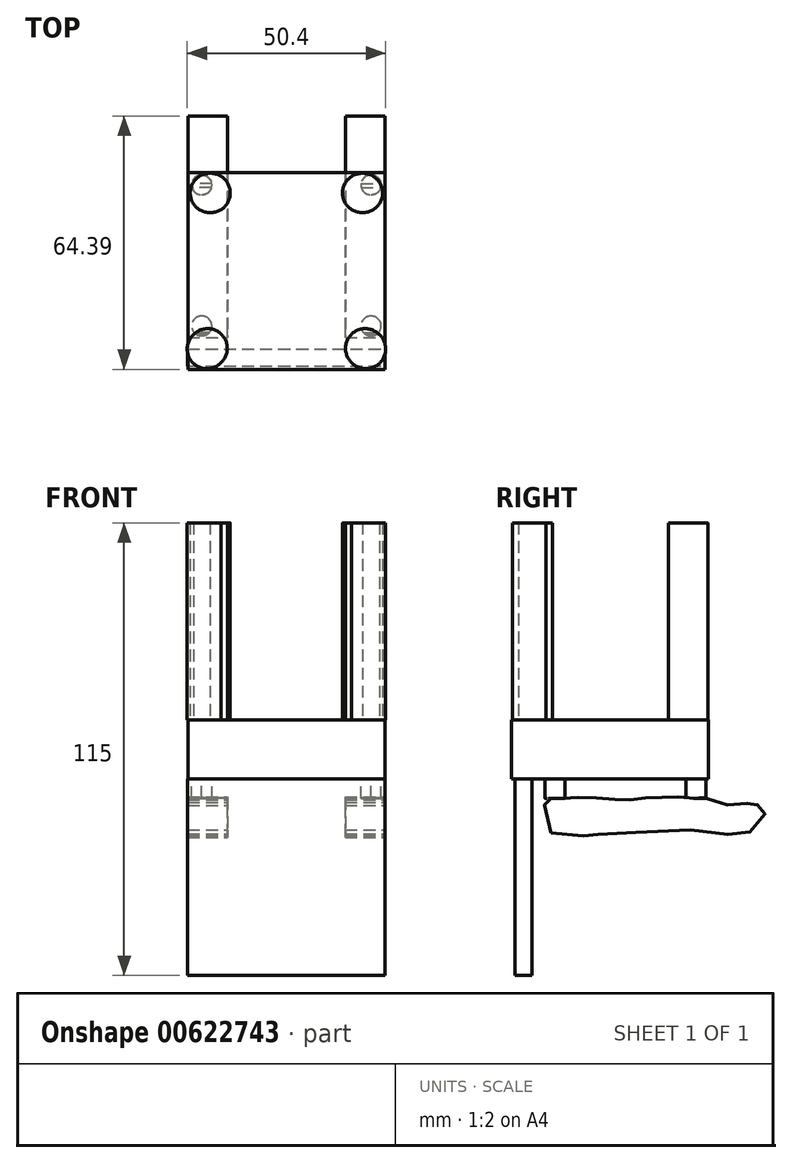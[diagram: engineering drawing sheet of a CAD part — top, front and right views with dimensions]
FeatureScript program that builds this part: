
annotation { "Feature Type Name" : "Feature", "Feature Type Description" : "" }
export const myFeature = defineFeature(function(context is Context, id is Id, definition is map)
    precondition{}
    {
        {
            var Q0;
            Q0=qCreatedBy(makeId("Top.planeOp"),FACE);
            var sketch = newSketch(context, id + "F0", { "sketchPlane" : qUnion([Q0])});
            skLineSegment(sketch, "E0.bottom", {"start": v(-25, 25) * mm, "end": v(25, 25) * mm});
            skLineSegment(sketch, "E0.top", {"start": v(-25, -25) * mm, "end": v(25, -25) * mm});
            skLineSegment(sketch, "E0.left", {"start": v(-25, 25) * mm, "end": v(-25, -25) * mm});
            skLineSegment(sketch, "E0.right", {"start": v(25, 25) * mm, "end": v(25, -25) * mm});
            skPoint(sketch, "E0.middle", {"position": v(0, 0) * mm});
            skSolve(sketch);
        }
        {
            var Q0;
            Q0 = qSketchRegion(id + "F0", true);
            extrude(context, id + "F1", {"entities" : qUnion([Q0]), "depth" : 15 * mm, "offsetDistance" : 25 * mm});
        }
        {
            var Q0;
            Q0=makeQuery(id+"F1.opExtrude","CAP_FACE",FACE,{"disambiguationData":[OSD([sQuery(id+"F0.wireOp",EDGE,"E0.bottom"),sQuery(id+"F0.wireOp",EDGE,"E0.top"),sQuery(id+"F0.wireOp",EDGE,"E0.left"),sQuery(id+"F0.wireOp",EDGE,"E0.right")])],"isStart":false});
            var sketch = newSketch(context, id + "F2", { "sketchPlane" : qUnion([Q0])});
            skCircle(sketch, "E1", {"center": v(-19.45, 19.83) * mm, "radius": 5 * mm});
            skCircle(sketch, "E2", {"center": v(19.26, 19.83) * mm, "radius": 5 * mm});
            skCircle(sketch, "E3", {"center": v(20.02, -19.64) * mm, "radius": 5 * mm});
            skCircle(sketch, "E4", {"center": v(-20.2, -19.83) * mm, "radius": 5 * mm});
            skSolve(sketch);
        }
        {
            var Q0;
            Q0=makeQuery(id+"F2.imprint","IMPRINT",FACE,{"disambiguationData":[TD([[makeQuery(id+"F2.imprint","IMPRINT",EDGE,{"derivedFrom":sQuery(id+"F2.wireOp",EDGE,"E1")}),1.0]])]});
            extrude(context, id + "F3", {"entities" : qUnion([Q0]), "operationType" : NewBodyOperationType.ADD, "depth" : 50 * mm, "offsetDistance" : 25 * mm});
        }
        {
            var Q0;
            Q0 = qSketchRegion(id + "F2", true);
            extrude(context, id + "F4", {"entities" : qUnion([Q0]), "operationType" : NewBodyOperationType.ADD, "depth" : 50 * mm, "offsetDistance" : 25 * mm});
        }
        {
            var Q0;
            Q0=qCreatedBy(makeId("Top.planeOp"),FACE);
            var sketch = newSketch(context, id + "F5", { "sketchPlane" : qUnion([Q0])});
            skLineSegment(sketch, "E5.bottom", {"start": v(-24.9, -24.15) * mm, "end": v(25.1, -24.15) * mm});
            skLineSegment(sketch, "E5.top", {"start": v(-24.9, -19.83) * mm, "end": v(25.1, -19.83) * mm});
            skLineSegment(sketch, "E5.left", {"start": v(-24.9, -24.15) * mm, "end": v(-24.9, -19.83) * mm});
            skLineSegment(sketch, "E5.right", {"start": v(25.1, -24.15) * mm, "end": v(25.1, -19.83) * mm});
            skSolve(sketch);
        }
        {
            var Q0;
            Q0 = qSketchRegion(id + "F5", true);
            extrude(context, id + "F6", {"entities" : qUnion([Q0]), "operationType" : NewBodyOperationType.ADD, "oppositeDirection" : true, "depth" : 50 * mm, "offsetDistance" : 25 * mm});
        }
        {
            var Q0;
            Q0=qCreatedBy(makeId("Top.planeOp"),FACE);
            var sketch = newSketch(context, id + "F7", { "sketchPlane" : qUnion([Q0])});
            skCircle(sketch, "E6", {"center": v(-21.58, -13.95) * mm, "radius": 2.5 * mm});
            skCircle(sketch, "E7", {"center": v(-21.58, 21.86) * mm, "radius": 2.5 * mm});
            skCircle(sketch, "E8", {"center": v(21.44, 21.86) * mm, "radius": 2.5 * mm});
            skCircle(sketch, "E9", {"center": v(21.44, -13.95) * mm, "radius": 2.5 * mm});
            skSolve(sketch);
        }
        {
            var Q0;
            Q0 = qSketchRegion(id + "F7", true);
            extrude(context, id + "F8", {"entities" : qUnion([Q0]), "operationType" : NewBodyOperationType.ADD, "oppositeDirection" : true, "depth" : 5 * mm, "offsetDistance" : 25 * mm});
        }
        {
            var Q0;
            Q0=qCreatedBy(makeId("Right.planeOp"),FACE);
            cPlane(context, id + "F9", {"entities" : qUnion([Q0]), "cplaneType" : CPlaneType.OFFSET, "offset" : 25 * mm, "oppositeDirection" : true, "width" : 150 * mm, "height" : 150 * mm});
        }
        {
            var Q0;
            Q0=qCreatedBy(id+"F9.planeOp",FACE);
            var sketch = newSketch(context, id + "F10", { "sketchPlane" : qUnion([Q0])});
            skFitSpline(sketch, "E10", {"points": [v(-14.99, -13.8) * mm, v(-3.76, -13.96) * mm, v(-3.5, -14.1) * mm, v(23.89, -13.2) * mm, v(34.71, -14.04) * mm, v(39.38, -8.64) * mm, v(37.77, -7.04) * mm, v(37.1, -6.1) * mm, v(34.57, -6.3) * mm, v(28.96, -6.57) * mm, v(23.9, -4.85) * mm, v(22.02, -5.01) * mm, v(18.01, -4.7) * mm, v(14.07, -4.76) * mm, v(10.64, -4.62) * mm, v(6.38, -5.31) * mm, v(3.84, -5.24) * mm, v(0, -5.19) * mm, v(-5.25, -4.76) * mm, v(-9.52, -4.86) * mm, v(-12.6, -5.07) * mm, v(-14.87, -5.12) * mm, v(-15.4, -5.13) * mm, v(-16.07, -5) * mm, v(-14.99, -13.8) * mm]});
            skSolve(sketch);
        }
        {
            var Q0;
            Q0=makeQuery(id+"F10.imprint","IMPRINT",FACE,{"disambiguationData":[TD([[makeQuery(id+"F10.imprint","IMPRINT",EDGE,{"derivedFrom":sQuery(id+"F10.wireOp",EDGE,"E10")}),1.0]])]});
            extrude(context, id + "F11", {"entities" : qUnion([Q0]), "operationType" : NewBodyOperationType.ADD, "depth" : 10 * mm, "offsetDistance" : 25 * mm});
        }
        {
            var Q0;
            Q0=makeQuery(id+"F1.opExtrude","SWEPT_BODY",BODY,{"disambiguationData":[OSD([sQuery(id+"F0.wireOp",EDGE,"E0.bottom"),sQuery(id+"F0.wireOp",EDGE,"E0.top"),sQuery(id+"F0.wireOp",EDGE,"E0.left"),sQuery(id+"F0.wireOp",EDGE,"E0.right")])]});
            var Q1;
            Q1=qCreatedBy(makeId("Right.planeOp"),FACE);
            mirror(context, id + "F12", {"operationType" : NewBodyOperationType.ADD, "entities" : qUnion([Q0]), "mirrorPlane" : qUnion([Q1])});
        }
    });
